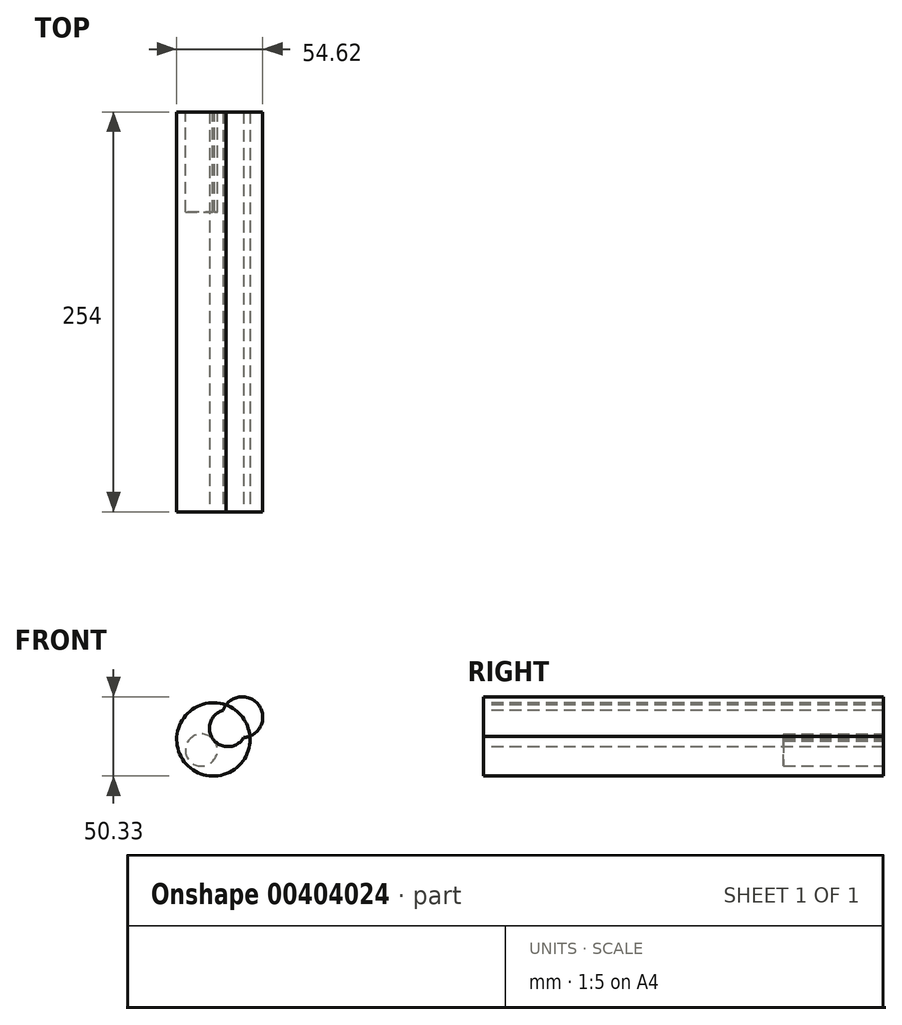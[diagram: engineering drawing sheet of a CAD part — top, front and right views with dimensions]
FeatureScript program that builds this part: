
annotation { "Feature Type Name" : "Feature", "Feature Type Description" : "" }
export const myFeature = defineFeature(function(context is Context, id is Id, definition is map)
    precondition{}
    {
        {
            var Q0;
            Q0=qCreatedBy(makeId("Front.planeOp"),FACE);
            var sketch = newSketch(context, id + "F0", { "sketchPlane" : qUnion([Q0])});
            skCircle(sketch, "E0", {"center": v(0, 0) * mm, "radius": 23.26 * mm});
            skCircle(sketch, "E1", {"center": v(9.2, 7.06) * mm, "radius": 11.67 * mm});
            skCircle(sketch, "E2", {"center": v(18.4, 14.11) * mm, "radius": 12.96 * mm});
            skSolve(sketch);
        }
        {
            var Q0;
            {var subQ0=sQuery(id+"F0.wireOp",EDGE,"E2");var subQ1=sQuery(id+"F0.wireOp",EDGE,"E0");var subQ2=makeQuery(id+"F0.imprint","INTERSECT",VERTEX,{"disambiguationData":[OD(0.0)],"derivedFrom":[subQ1,subQ0]});Q0=makeQuery(id+"F0.imprint","IMPRINT",FACE,{"disambiguationData":[TD([[makeQuery(id+"F0.imprint","IMPRINT",EDGE,{"disambiguationData":[TD([[subQ2,1.0]])],"derivedFrom":subQ1}),1.0]])]});}
            var Q1;
            {var subQ0=sQuery(id+"F0.wireOp",EDGE,"E2");var subQ1=sQuery(id+"F0.wireOp",EDGE,"E0");var subQ2=makeQuery(id+"F0.imprint","INTERSECT",VERTEX,{"disambiguationData":[OD(0.0)],"derivedFrom":[subQ1,subQ0]});Q1=makeQuery(id+"F0.imprint","IMPRINT",FACE,{"disambiguationData":[TD([[makeQuery(id+"F0.imprint","IMPRINT",EDGE,{"disambiguationData":[TD([[subQ2,-1.0]])],"derivedFrom":subQ1}),-1.0]])]});}
            extrude(context, id + "F1", {"entities" : qUnion([Q0, Q1]), "oppositeDirection" : true, "depth" : 254 * mm});
        }
        {
            var Q0;
            Q0=makeQuery(id+"F1.opExtrude","CAP_FACE",FACE,{"disambiguationData":[OSD([sQuery(id+"F0.wireOp",EDGE,"E0"),sQuery(id+"F0.wireOp",EDGE,"E1"),sQuery(id+"F0.wireOp",EDGE,"E2")])],"isStart":false});
            var sketch = newSketch(context, id + "F2", { "sketchPlane" : qUnion([Q0])});
            skCircle(sketch, "E3", {"center": v(7.6, -6.77) * mm, "radius": 10.18 * mm});
            skSolve(sketch);
        }
        {
            var Q0;
            Q0 = qSketchRegion(id + "F2", true);
            extrude(context, id + "F3", {"entities" : qUnion([Q0]), "operationType" : NewBodyOperationType.REMOVE, "oppositeDirection" : true, "depth" : 63.5 * mm});
        }
    });
